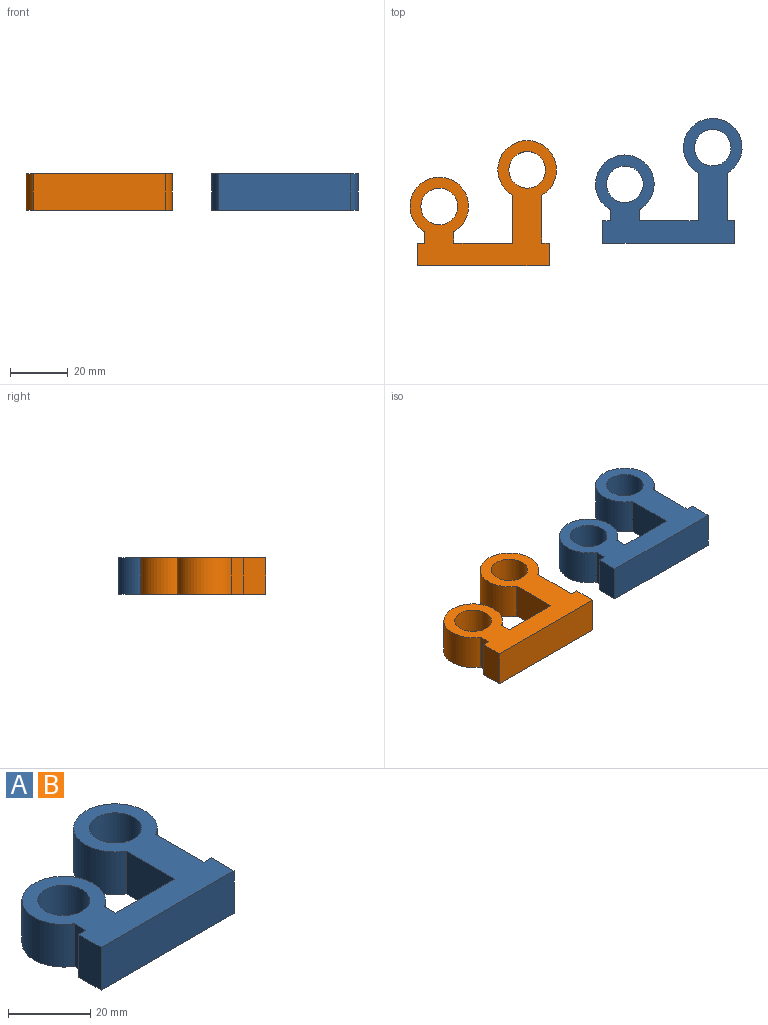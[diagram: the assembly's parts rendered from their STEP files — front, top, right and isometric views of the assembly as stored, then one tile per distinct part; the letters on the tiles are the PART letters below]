
ASSEMBLY  parts=2 mates=1
PART A: 16 faces, bbox 50.8x43.4x12.7 mm
  f0: plane 12.7x3.9mm, normal (1,0,0), area 49.5mm2, adj f1,f13,f14,f15
  f1: cylinder r=10.16mm len=20.32mm, axis (0,0,-1), area 675.6mm2, adj f0,f2,f14,f15
  f2: plane 12.7x3.9mm, normal (-1,0,0), area 49.5mm2, adj f1,f3,f14,f15
  f3: plane 12.7x2.54mm, normal (0,1,0), area 32.3mm2, adj f2,f4,f14,f15
  f4: plane 12.7x7.8mm, normal (-1,0,0), area 99.1mm2, adj f3,f5,f14,f15
  f5: plane 45.72x12.7mm, normal (0,-1,0), area 580.6mm2, adj f4,f6,f14,f15
  f6: plane 12.7x7.8mm, normal (1,0,0), area 99.1mm2, adj f5,f7,f14,f15
  f7: plane 12.7x2.54mm, normal (0,1,0), area 32.3mm2, adj f6,f8,f14,f15
  f8: plane 16.6x12.7mm, normal (1,0,0), area 210.8mm2, adj f7,f9,f14,f15
  f9: cylinder r=10.16mm len=20.32mm, axis (0,0,-1), area 675.6mm2, adj f8,f10,f14,f15
  f10: plane 16.6x12.7mm, normal (-1,0,0), area 210.8mm2, adj f9,f13,f14,f15
  f11: cylinder r=6.35mm len=12.7mm, axis (0,0,-1), area 506.7mm2, adj f14,f15
  f12: cylinder r=6.35mm len=12.7mm, axis (0,0,-1), area 506.7mm2, adj f14,f15
  f13: plane 20.32x12.7mm, normal (0,1,0), area 258.1mm2, adj f0,f10,f14,f15
  f14: plane 50.8x43.36mm, normal (0,0,1), area 941.4mm2, adj f0,f1,f2,f3,f4,f5,f6,f7
  f15: plane 50.8x43.36mm, normal (0,0,-1), area 941.4mm2, adj f0,f1,f2,f3,f4,f5,f6,f7
PART B: same geometry as A
PLACE A t=(-0.45,-7.96,8.78)mm fixed
PLACE B t=(-64.8,-15.65,8.78)mm
MATE planar B.f9 <-> A.f1  axis (0,0,-1) through (-49.56,13.65,8.78)mm
